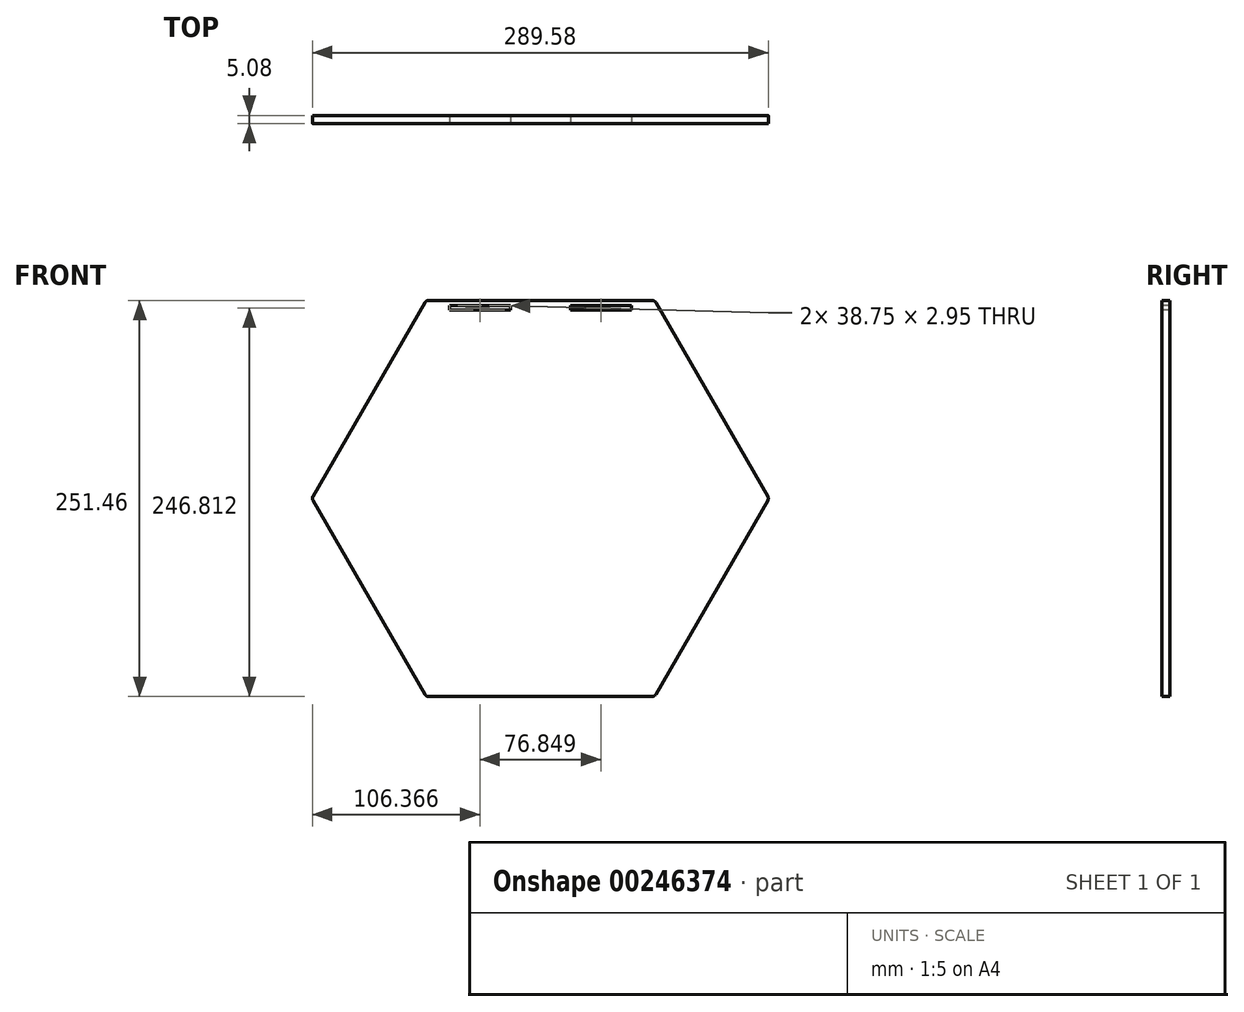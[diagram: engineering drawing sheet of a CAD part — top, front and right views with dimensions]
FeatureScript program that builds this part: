
annotation { "Feature Type Name" : "Feature", "Feature Type Description" : "" }
export const myFeature = defineFeature(function(context is Context, id is Id, definition is map)
    precondition{}
    {
        {
            var Q0;
            Q0=qCreatedBy(makeId("Front.planeOp"),FACE);
            var sketch = newSketch(context, id + "F0", { "sketchPlane" : qUnion([Q0])});
            skCircle(sketch, "E0.cCircle", {"center": v(0, 0) * mm, "radius": 125.73 * mm, "construction": true});
            skLineSegment(sketch, "E0.0", {"start": v(-71.12, 125.73) * mm, "end": v(71.12, 125.73) * mm});
            skLineSegment(sketch, "E0.1", {"start": v(73.32, 124.46) * mm, "end": v(144.45, 1.27) * mm});
            skLineSegment(sketch, "E0.2", {"start": v(144.45, -1.27) * mm, "end": v(73.32, -124.46) * mm});
            skLineSegment(sketch, "E0.3", {"start": v(71.12, -125.73) * mm, "end": v(-71.12, -125.73) * mm});
            skLineSegment(sketch, "E0.4", {"start": v(-73.32, -124.46) * mm, "end": v(-144.45, -1.27) * mm});
            skLineSegment(sketch, "E0.5", {"start": v(-144.45, 1.27) * mm, "end": v(-73.32, 124.46) * mm});
            skPoint(sketch, "E0.0.midPoint", {"position": v(0, 125.73) * mm});
            skPoint(sketch, "E1.visualSharp", {"position": v(-72.6, 125.73) * mm});
            skArc(sketch, "E1.filletArc", {"start": v(-71.12, 125.73) * mm, "mid": v(-72.4, 125.39) * mm, "end": v(-73.32, 124.46) * mm});
            skPoint(sketch, "E2.visualSharp", {"position": v(72.6, 125.73) * mm});
            skArc(sketch, "E2.filletArc", {"start": v(73.32, 124.46) * mm, "mid": v(72.4, 125.39) * mm, "end": v(71.12, 125.73) * mm});
            skPoint(sketch, "E3.visualSharp", {"position": v(145.18, 0) * mm});
            skArc(sketch, "E3.filletArc", {"start": v(144.45, -1.27) * mm, "mid": v(144.79, 0) * mm, "end": v(144.45, 1.27) * mm});
            skPoint(sketch, "E4.visualSharp", {"position": v(72.6, -125.73) * mm});
            skArc(sketch, "E4.filletArc", {"start": v(71.12, -125.73) * mm, "mid": v(72.4, -125.39) * mm, "end": v(73.32, -124.46) * mm});
            skPoint(sketch, "E5.visualSharp", {"position": v(-72.6, -125.73) * mm});
            skArc(sketch, "E5.filletArc", {"start": v(-73.32, -124.46) * mm, "mid": v(-72.4, -125.39) * mm, "end": v(-71.12, -125.73) * mm});
            skPoint(sketch, "E6.visualSharp", {"position": v(-145.18, 0) * mm});
            skArc(sketch, "E6.filletArc", {"start": v(-144.45, 1.27) * mm, "mid": v(-144.79, 0) * mm, "end": v(-144.45, -1.27) * mm});
            skSolve(sketch);
        }
        {
            var Q0;
            Q0=makeQuery(id+"F0.imprint","IMPRINT",FACE,{"disambiguationData":[TD([[makeQuery(id+"F0.imprint","IMPRINT",EDGE,{"derivedFrom":sQuery(id+"F0.wireOp",EDGE,"E0.0")}),-1.0]])]});
            extrude(context, id + "F1", {"entities" : qUnion([Q0]), "depth" : 5.08 * mm});
        }
        {
            var Q0;
            Q0=makeQuery(id+"F1.opExtrude","CAP_FACE",FACE,{"disambiguationData":[OSD([sQuery(id+"F0.wireOp",EDGE,"E0.0"),sQuery(id+"F0.wireOp",EDGE,"E0.1"),sQuery(id+"F0.wireOp",EDGE,"E0.2"),sQuery(id+"F0.wireOp",EDGE,"E0.3"),sQuery(id+"F0.wireOp",EDGE,"E0.4"),sQuery(id+"F0.wireOp",EDGE,"E0.5"),sQuery(id+"F0.wireOp",EDGE,"E1.filletArc"),sQuery(id+"F0.wireOp",EDGE,"E2.filletArc"),sQuery(id+"F0.wireOp",EDGE,"E3.filletArc"),sQuery(id+"F0.wireOp",EDGE,"E4.filletArc"),sQuery(id+"F0.wireOp",EDGE,"E5.filletArc"),sQuery(id+"F0.wireOp",EDGE,"E6.filletArc")])],"isStart":false});
            var sketch = newSketch(context, id + "F2", { "sketchPlane" : qUnion([Q0])});
            skCircle(sketch, "E7.cCircle", {"center": v(0, 0) * mm, "radius": 125.73 * mm, "construction": true});
            skLineSegment(sketch, "E7.0", {"start": v(-57.93, 125.73) * mm, "end": v(57.93, 125.73) * mm, "construction": true});
            skLineSegment(sketch, "E7.1", {"start": v(79.92, 113.03) * mm, "end": v(137.85, 12.7) * mm, "construction": true});
            skLineSegment(sketch, "E7.2", {"start": v(137.85, -12.7) * mm, "end": v(79.92, -113.03) * mm, "construction": true});
            skLineSegment(sketch, "E7.3", {"start": v(57.93, -125.73) * mm, "end": v(-57.93, -125.73) * mm, "construction": true});
            skLineSegment(sketch, "E7.4", {"start": v(-79.92, -113.03) * mm, "end": v(-137.85, -12.7) * mm, "construction": true});
            skLineSegment(sketch, "E7.5", {"start": v(-137.85, 12.7) * mm, "end": v(-79.92, 113.03) * mm, "construction": true});
            skPoint(sketch, "E7.0.midPoint", {"position": v(0, 125.73) * mm});
            skPoint(sketch, "E8.visualSharp", {"position": v(-72.6, 125.73) * mm});
            skArc(sketch, "E8.filletArc", {"start": v(-57.93, 125.73) * mm, "mid": v(-70.63, 122.33) * mm, "end": v(-79.92, 113.03) * mm, "construction": true});
            skPoint(sketch, "E9.visualSharp", {"position": v(72.6, 125.73) * mm});
            skArc(sketch, "E9.filletArc", {"start": v(79.92, 113.03) * mm, "mid": v(70.63, 122.33) * mm, "end": v(57.93, 125.73) * mm, "construction": true});
            skPoint(sketch, "E10.visualSharp", {"position": v(145.18, 0) * mm});
            skArc(sketch, "E10.filletArc", {"start": v(137.85, -12.7) * mm, "mid": v(141.25, 0) * mm, "end": v(137.85, 12.7) * mm, "construction": true});
            skPoint(sketch, "E11.visualSharp", {"position": v(72.6, -125.73) * mm});
            skArc(sketch, "E11.filletArc", {"start": v(57.93, -125.73) * mm, "mid": v(70.63, -122.33) * mm, "end": v(79.92, -113.03) * mm, "construction": true});
            skPoint(sketch, "E12.visualSharp", {"position": v(-72.6, -125.73) * mm});
            skArc(sketch, "E12.filletArc", {"start": v(-79.92, -113.03) * mm, "mid": v(-70.63, -122.33) * mm, "end": v(-57.93, -125.73) * mm, "construction": true});
            skPoint(sketch, "E13.visualSharp", {"position": v(-145.18, 0) * mm});
            skArc(sketch, "E13.filletArc", {"start": v(-137.85, 12.7) * mm, "mid": v(-141.25, 0) * mm, "end": v(-137.85, -12.7) * mm, "construction": true});
            skLineSegment(sketch, "E14.bottom", {"start": v(-57.8, 122.56) * mm, "end": v(57.8, 122.56) * mm});
            skLineSegment(sketch, "E14.top", {"start": v(-57.8, 119.6) * mm, "end": v(57.8, 119.6) * mm});
            skLineSegment(sketch, "E14.left", {"start": v(-57.8, 122.56) * mm, "end": v(-57.8, 119.6) * mm});
            skLineSegment(sketch, "E14.right", {"start": v(57.8, 122.56) * mm, "end": v(57.8, 119.6) * mm});
            skLineSegment(sketch, "E15.bottom", {"start": v(-19.05, 122.56) * mm, "end": v(19.05, 122.56) * mm});
            skLineSegment(sketch, "E15.top", {"start": v(-19.05, 119.6) * mm, "end": v(19.05, 119.6) * mm});
            skLineSegment(sketch, "E15.left", {"start": v(-19.05, 122.56) * mm, "end": v(-19.05, 119.6) * mm});
            skLineSegment(sketch, "E15.right", {"start": v(19.05, 122.56) * mm, "end": v(19.05, 119.6) * mm});
            skPoint(sketch, "E16", {"position": v(0, 119.6) * mm});
            skSolve(sketch);
        }
        {
            var Q0;
            {var subQ0=sQuery(id+"F2.wireOp",EDGE,"E14.left");Q0=makeQuery(id+"F2.imprint","IMPRINT",FACE,{"disambiguationData":[TD([[makeQuery(id+"F2.imprint","IMPRINT",EDGE,{"derivedFrom":subQ0}),1.0]])]});}
            var Q1;
            {var subQ0=sQuery(id+"F2.wireOp",EDGE,"E14.right");Q1=makeQuery(id+"F2.imprint","IMPRINT",FACE,{"disambiguationData":[TD([[makeQuery(id+"F2.imprint","IMPRINT",EDGE,{"derivedFrom":subQ0}),-1.0]])]});}
            var Q2;
            Q2=makeQuery(id+"F1.opExtrude","CAP_FACE",FACE,{"disambiguationData":[OSD([sQuery(id+"F0.wireOp",EDGE,"E0.0"),sQuery(id+"F0.wireOp",EDGE,"E0.1"),sQuery(id+"F0.wireOp",EDGE,"E0.2"),sQuery(id+"F0.wireOp",EDGE,"E0.3"),sQuery(id+"F0.wireOp",EDGE,"E0.4"),sQuery(id+"F0.wireOp",EDGE,"E0.5"),sQuery(id+"F0.wireOp",EDGE,"E1.filletArc"),sQuery(id+"F0.wireOp",EDGE,"E2.filletArc"),sQuery(id+"F0.wireOp",EDGE,"E3.filletArc"),sQuery(id+"F0.wireOp",EDGE,"E4.filletArc"),sQuery(id+"F0.wireOp",EDGE,"E5.filletArc"),sQuery(id+"F0.wireOp",EDGE,"E6.filletArc")])],"isStart":true});
            extrude(context, id + "F3", {"entities" : qUnion([Q0, Q1]), "operationType" : NewBodyOperationType.REMOVE, "endBound" : BoundingType.UP_TO_SURFACE, "oppositeDirection" : true, "endBoundEntityFace" : qUnion([Q2]), "depth" : 25.4 * mm});
        }
        {
            var Q0;
            Q0=qCreatedBy(makeId("Right.planeOp"),FACE);
            var sketch = newSketch(context, id + "F4", { "sketchPlane" : qUnion([Q0])});
            skLineSegment(sketch, "E17", {"start": v(0, 0) * mm, "end": v(-126.56, 0) * mm, "construction": true});
            skSolve(sketch);
        }
    });
